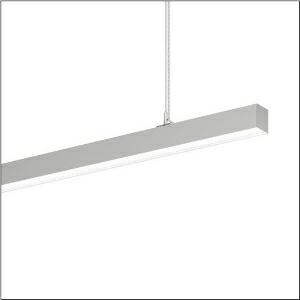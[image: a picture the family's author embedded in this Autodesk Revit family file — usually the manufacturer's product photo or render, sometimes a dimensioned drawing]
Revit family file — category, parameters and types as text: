
# Revit family: silica_r__21_51mx33dc4dsb_9471
name_source: partatom
category: Lighting Fixtures
units: mm (PartAtom-declared; Revit-internal decimal feet)

## family parameters
Cut with Voids When Loaded = No
Host = Face
Light Source = No
Part Type = Normal
Room Calculation Point = No
Round Connector Dimension = Use Diameter
Shared = No

## types (1)
- --- (1 x LED, 14790 lm, 93.9 W, 4000K)
    Apparent Load = 94 VA
    CIE Flux Codes = 78 96 99 55 100
    Color Rendering = 80
    Color Temperature = 4000K
    Default Elevation = 1800 mm
    Description = Silica® 21, office luminaire, primary optical cover: prismatic diffuser, of PMMA, CAT 2 (L<= 3000cd/m²), light emission: direct/indirect distribution, primary light characteristic: symmetric, installation type: suspended mounting, LED, rated luminous flux: 14.790lm, luminous efficacy: 158lm/W, light colour: 840, colour temperature: 4000K, control gear: DALI 2, with terminal, 3+2-pole, max. 2.5mm², mains connection: 220..240V, AC, 50/60Hz, rated input power: 93.9W, luminaire housing, of aluminium, metallic grey (RAL 9006), length: 3.004mm, width: 53mm, height: 53mm, protection rating (complete): IP20, insulation class (complete): insulation class I (protective earthing), certification: CE, permissible operating ambient temperature: 0..+35°C, standard: EN 50419, packaging unit: 1 piece
    Height = 53 mm
    Lamp = 1 x LED
    Lamp Light Flux = 14790 lm
    Lamp Power = 93.9 W
    Lamp count = 1
    Length = 3004 mm
    Luminous efficacy = 158 lm/W
    Manufacturer = Siteco
    ModVariant = No
    Model = 51MX33DC4DSB
    Mounting Place = Ceiling
    Mounting Type = Pendant
    Number of Poles = 1
    OnlyDefault = Yes
    Power Factor = 1
    Product Name = Silica® 21
    Product group = office luminaire | ceiling pendant
    ProductGroupID = 904
    Protection Class = Protection class I
    Protection Degree = IP 20
    RLX_Detail_Level = 1
    RLX_Emergency_Light_Flux = 0 lm
    RLX_Emergency_Type = 0
    RLX_Emergency_Type_DB = No
    RlxData = <blob elided: 23385 chars, md5=9a06e9d4>
    Socket = socket
    Standby Power = 0 W
    System Light Flux = 14790 lm
    System Power = 94 W
    Type Comments = factory setting: luminous flux: 100 % | dim-lin: 254 | 323 mA
    Type Image = l_1335864.jpg
    URL = http://relux.com
    VarID = @adj_118504
    Voltage = 0 V
    Weight = 0.00 kg
    Width = 53 mm

## geometry (parser evidence)
native form markers: Blend x4, Sweep x12
no freeform markers — native parametric forms only
